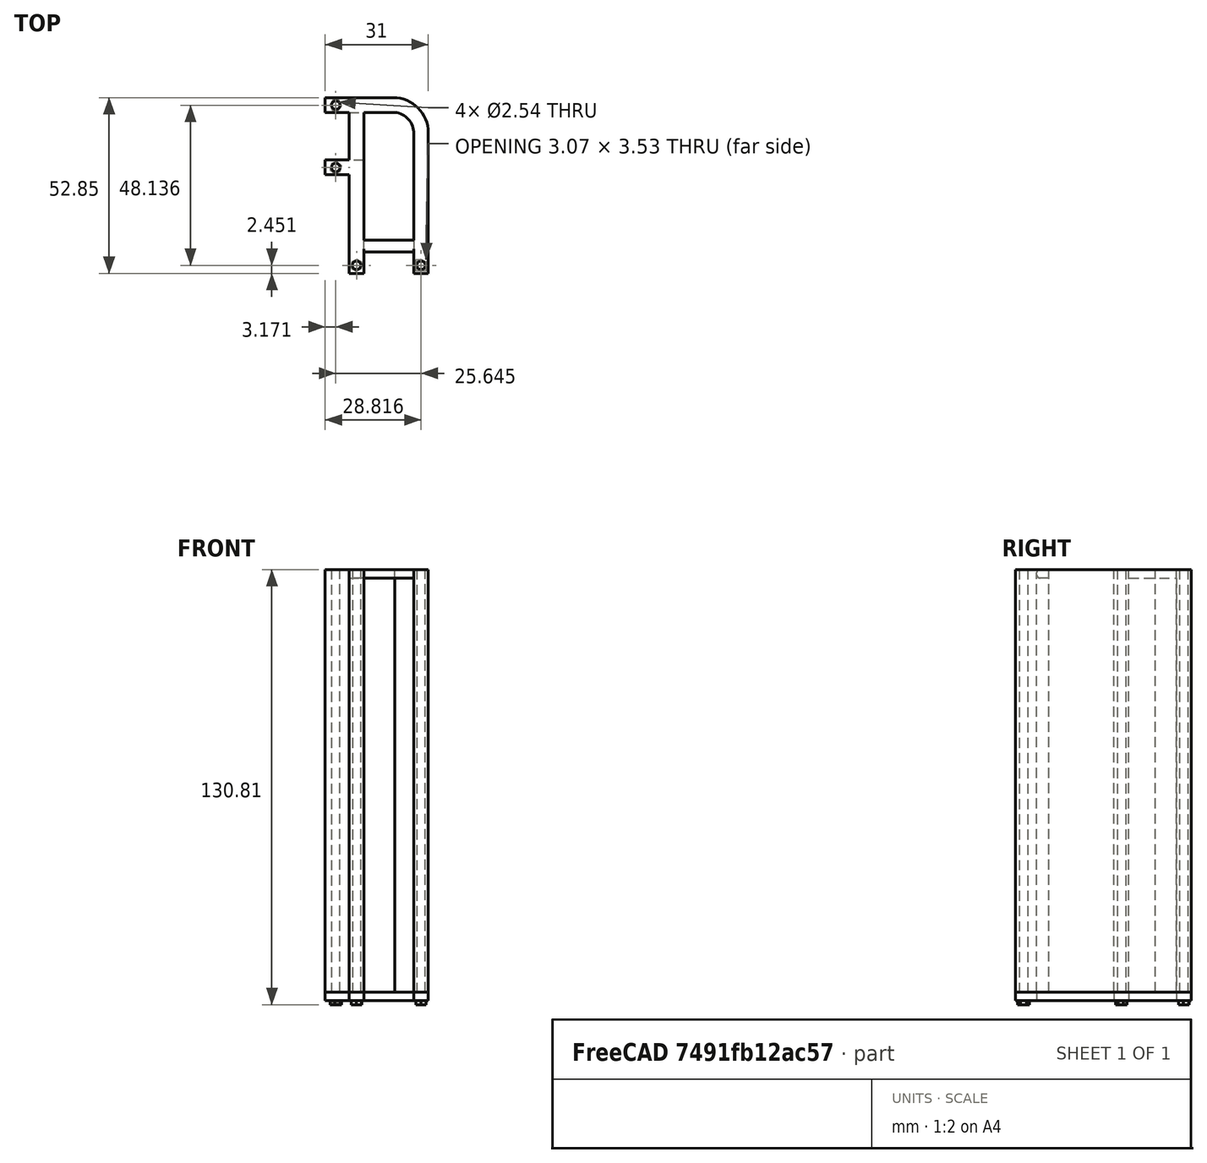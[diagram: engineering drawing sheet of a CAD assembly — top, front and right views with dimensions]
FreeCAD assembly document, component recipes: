
FREECAD ASSEMBLY — COMPONENT RECIPES ("mrscoopy_test")

This assembly document has 2 components, labeled P0..P1 below (a component is one placed body or linked part). 2 of them carry a construction recipe — the FreeCAD feature program that regenerates the part from scratch, quoted from this document or its linked companion documents; the rest are supplied as boundary geometry only. No exploded tour is included for this assembly.
COMPONENT P0 — recipe-attached ("Body", modeled in this document).
Construction recipe (the document's own serialized feature program — sketch geometry with constraints, then the solid features built on it; lengths are millimeters unless a unit is written):

FEATURE [Sketcher::SketchObject] Sketch
  FullyConstrained = false
  MapMode = 5
  Support = -> [XY_Plane]
  sketch-geometry (26):
    g0: LineSegment StartX=0 StartY=26.6063 StartZ=0 EndX=-7.16788 EndY=26.6063 EndZ=0
    g1: LineSegment StartX=-7.16788 StartY=26.6063 StartZ=0 EndX=-7.16788 EndY=31.0413 EndZ=0
    g2: LineSegment StartX=-7.16788 StartY=31.0413 StartZ=0 EndX=13.2403 EndY=31.0413 EndZ=0
    g3: ArcOfCircle CenterX=13.2403 CenterY=20.4538 CenterZ=0 NormalX=0 NormalY=0 NormalZ=1 AngleXU=0 Radius=10.5875 StartAngle=2e-16 EndAngle=1.5708
    g4: LineSegment StartX=23.8278 StartY=20.4538 StartZ=0 EndX=23.8278 EndY=-21.8072 EndZ=0
    g5: LineSegment StartX=23.8278 StartY=-21.8072 StartZ=0 EndX=19.3928 EndY=-21.8072 EndZ=0
    g6: LineSegment StartX=19.3928 StartY=-21.8072 StartZ=0 EndX=19.3928 EndY=-15.4126 EndZ=0
    g7: LineSegment StartX=19.3928 StartY=-15.4126 StartZ=0 EndX=4.43503 EndY=-15.4126 EndZ=0
    g8: LineSegment StartX=4.43503 StartY=-15.4126 StartZ=0 EndX=4.43503 EndY=-21.78 EndZ=0
    g9: LineSegment StartX=4.43503 StartY=-21.78 StartZ=0 EndX=0 EndY=-21.78 EndZ=0
    g10: LineSegment StartX=0 StartY=26.6063 StartZ=0 EndX=0 EndY=12.274 EndZ=0
    g11: LineSegment StartX=0 StartY=12.274 StartZ=0 EndX=-7.16788 EndY=12.274 EndZ=0
    g12: LineSegment StartX=-7.16788 StartY=12.274 StartZ=0 EndX=-7.16788 EndY=7.839 EndZ=0
    g13: LineSegment StartX=-7.16788 StartY=7.839 StartZ=0 EndX=0 EndY=7.839 EndZ=0
    g14: LineSegment StartX=0 StartY=7.839 StartZ=0 EndX=0 EndY=-21.78 EndZ=0
    g15: LineSegment StartX=19.3928 StartY=20.1836 StartZ=0 EndX=19.3928 EndY=-11.8217 EndZ=0
    g16: LineSegment StartX=19.3928 StartY=-11.8217 StartZ=0 EndX=4.43503 EndY=-11.8217 EndZ=0
    g17: LineSegment StartX=4.43503 StartY=-11.8217 StartZ=0 EndX=4.43503 EndY=26.5927 EndZ=0
    g18: LineSegment StartX=4.43503 StartY=26.5927 StartZ=0 EndX=13.7304 EndY=26.5927 EndZ=0
    g19: ArcOfCircle CenterX=13.2403 CenterY=20.4538 CenterZ=0 NormalX=0 NormalY=0 NormalZ=1 AngleXU=0 Radius=6.15845 StartAngle=6.23931 EndAngle=7.77431
    g20: Circle CenterX=-3.99854 CenterY=28.777 CenterZ=0 NormalX=0 NormalY=0 NormalZ=1 AngleXU=0 Radius=1.27118
    g21: Circle CenterX=-3.99854 CenterY=10.0357 CenterZ=0 NormalX=0 NormalY=0 NormalZ=1 AngleXU=0 Radius=1.27118
    g22: Circle CenterX=2.26851 CenterY=-19.3586 CenterZ=0 NormalX=0 NormalY=0 NormalZ=1 AngleXU=0 Radius=1.27118
    g23: Circle CenterX=21.6462 CenterY=-19.3586 CenterZ=0 NormalX=0 NormalY=0 NormalZ=1 AngleXU=0 Radius=1.27118
    g24: LineSegment StartX=2.26851 StartY=-19.3586 StartZ=0 EndX=21.6462 EndY=-19.3586 EndZ=0
    g25: LineSegment StartX=-3.99854 StartY=10.0357 StartZ=0 EndX=-3.99854 EndY=28.777 EndZ=0
  constraints (55):
    c: PointOnObject(g0,g-2)
    c: Horizontal(g0)
    c: Coincident(g0,g1)
    c: Vertical(g1)
    c: Coincident(g1,g2)
    c: Horizontal(g2)
    c: Coincident(g3,g2)
    c: Tangent(g3,g4) = 1.5708
    c: Coincident(g4,g5)
    c: Horizontal(g5)
    c: Coincident(g5,g6)
    c: Vertical(g6)
    c: Coincident(g6,g7)
    c: Horizontal(g7)
    c: Coincident(g7,g8)
    c: Vertical(g8)
    c: Coincident(g8,g9)
    c: PointOnObject(g9,g-2)
    c: Horizontal(g9)
    c: Vertical(g4)
    c: Equal(g5,g9)
    c: Equal(g1,g5)
    c: Tangent(g3,g2)
    c: Coincident(g0,g10)
    c: PointOnObject(g10,g-2)
    c: Coincident(g10,g11)
    c: Horizontal(g11)
    c: Coincident(g11,g12)
    c: Vertical(g12)
    c: Coincident(g12,g13)
    c: PointOnObject(g13,g-2)
    c: Horizontal(g13)
    c: Coincident(g14,g9)
    c: Coincident(g15,g16)
    c: Horizontal(g16)
    c: Coincident(g16,g17)
    c: Coincident(g18,g17)
    c: Horizontal(g18)
    c: Coincident(g19,g3)
    c: Coincident(g19,g18)
    c: Coincident(g19,g15)
    c: Tangent(g17,g8)
    c: Tangent(g15,g6)
    c: Equal(g0,g11)
    c: Equal(g12,g1)
    c: Equal(g20,g21)
    c: Equal(g20,g22)
    c: Equal(g20,g23)
    c: Coincident(g24,g22)
    c: Coincident(g24,g23)
    c: Horizontal(g24)
    c: Coincident(g25,g21)
    c: Coincident(g25,g20)
    c: Vertical(g25)
    c: Coincident(g14,g13)
FEATURE [PartDesign::Pad] Pad
  Direction = (0,0,1)
  Length = 127
  Length2 = 10
  Profile = -> Sketch
  ReferenceAxis = -> Sketch [N_Axis]
  Type = 0
FEATURE [Sketcher::SketchObject] Sketch001
  FullyConstrained = false
  MapMode = 5
  Support = -> [XY_Plane]
  sketch-geometry (8):
    g0: LineSegment StartX=0 StartY=26.6033 StartZ=0 EndX=4.4361 EndY=26.6033 EndZ=0
    g1: LineSegment StartX=4.4361 StartY=26.6033 StartZ=0 EndX=4.4361 EndY=12.2559 EndZ=0
    g2: LineSegment StartX=4.4361 StartY=12.2559 StartZ=0 EndX=0 EndY=12.2559 EndZ=0
    g3: LineSegment StartX=0 StartY=12.2559 StartZ=0 EndX=0 EndY=26.6033 EndZ=0
    g4: LineSegment StartX=4.4361 StartY=-11.8217 StartZ=0 EndX=19.3928 EndY=-11.8217 EndZ=0
    g5: LineSegment StartX=19.3928 StartY=-11.8217 StartZ=0 EndX=19.3928 EndY=-15.4126 EndZ=0
    g6: LineSegment StartX=19.3928 StartY=-15.4126 StartZ=0 EndX=4.4361 EndY=-15.4126 EndZ=0
    g7: LineSegment StartX=4.4361 StartY=-15.4126 StartZ=0 EndX=4.4361 EndY=-11.8217 EndZ=0
  constraints (17):
    c: PointOnObject(g0,g-2)
    c: Coincident(g0,g1)
    c: Coincident(g1,g2)
    c: Coincident(g2,g3)
    c: Coincident(g3,g0)
    c: Horizontal(g0)
    c: Horizontal(g2)
    c: Vertical(g1)
    c: Vertical(g3)
    c: Coincident(g4,g5)
    c: Coincident(g5,g6)
    c: Coincident(g6,g7)
    c: Coincident(g7,g4)
    c: Horizontal(g4)
    c: Horizontal(g6)
    c: Vertical(g5)
    c: Vertical(g7)
FEATURE [PartDesign::Pocket] Pocket
  BaseFeature = -> Pad
  Direction = (0,0,-1)
  Length = 124.46
  Length2 = 5
  Profile = -> Sketch001
  ReferenceAxis = -> Sketch001 [N_Axis]
  Reversed = true
  Type = 0
FEATURE [PartDesign::CoordinateSystem] Local_CS
  AttacherType = Attacher::AttachEngine3D
  MapMode = 5
  Support = -> [XY_Plane]
FEATURE [PartDesign::Fillet] Fillet
  Base = -> Pocket [Edge72,Edge31]
  BaseFeature = -> Pocket
  Radius = 0.9906
  SupportTransform = false
  UseAllEdges = false
FEATURE [PartDesign::Body] Body
  Group = -> [Sketch,Pad,Sketch001,Pocket,Local_CS,Fillet]
  Origin = -> Origin
  Tip = -> Fillet
COMPONENT P1 — recipe-attached ("Body004", modeled in this document).
Construction recipe (the document's own serialized feature program — sketch geometry with constraints, then the solid features built on it; lengths are millimeters unless a unit is written):

FEATURE [Sketcher::SketchObject] Sketch003
  FullyConstrained = false
  MapMode = 5
  Support = -> [XY_Plane002]
  sketch-geometry (21):
    g0: LineSegment StartX=0 StartY=26.6063 StartZ=0 EndX=-7.16788 EndY=26.6063 EndZ=0
    g1: LineSegment StartX=-7.16788 StartY=26.6063 StartZ=0 EndX=-7.16788 EndY=31.0413 EndZ=0
    g2: LineSegment StartX=-7.16788 StartY=31.0413 StartZ=0 EndX=13.2403 EndY=31.0413 EndZ=0
    g3: ArcOfCircle CenterX=13.2403 CenterY=20.4538 CenterZ=0 NormalX=0 NormalY=0 NormalZ=1 AngleXU=0 Radius=10.5875 StartAngle=2e-16 EndAngle=1.5708
    g4: LineSegment StartX=23.8278 StartY=20.4538 StartZ=0 EndX=23.8278 EndY=-21.8072 EndZ=0
    g5: LineSegment StartX=23.8278 StartY=-21.8072 StartZ=0 EndX=19.3928 EndY=-21.8072 EndZ=0
    g6: LineSegment StartX=19.3928 StartY=-21.8072 StartZ=0 EndX=19.3928 EndY=-15.4126 EndZ=0
    g7: LineSegment StartX=19.3928 StartY=-15.4126 StartZ=0 EndX=4.43503 EndY=-15.4126 EndZ=0
    g8: LineSegment StartX=4.43503 StartY=-15.4126 StartZ=0 EndX=4.43503 EndY=-21.78 EndZ=0
    g9: LineSegment StartX=4.43503 StartY=-21.78 StartZ=0 EndX=0 EndY=-21.78 EndZ=0
    g10: LineSegment StartX=0 StartY=26.6063 StartZ=0 EndX=0 EndY=12.274 EndZ=0
    g11: LineSegment StartX=0 StartY=12.274 StartZ=0 EndX=-7.16788 EndY=12.274 EndZ=0
    g12: LineSegment StartX=-7.16788 StartY=12.274 StartZ=0 EndX=-7.16788 EndY=7.839 EndZ=0
    g13: LineSegment StartX=-7.16788 StartY=7.839 StartZ=0 EndX=0 EndY=7.839 EndZ=0
    g14: LineSegment StartX=0 StartY=7.839 StartZ=0 EndX=0 EndY=-21.78 EndZ=0
    g15: Circle CenterX=-3.99854 CenterY=28.777 CenterZ=0 NormalX=0 NormalY=0 NormalZ=1 AngleXU=0 Radius=1.27118
    g16: Circle CenterX=-3.99854 CenterY=10.0357 CenterZ=0 NormalX=0 NormalY=0 NormalZ=1 AngleXU=0 Radius=1.27118
    g17: Circle CenterX=2.26851 CenterY=-19.3586 CenterZ=0 NormalX=0 NormalY=0 NormalZ=1 AngleXU=0 Radius=1.27118
    g18: Circle CenterX=21.6462 CenterY=-19.3586 CenterZ=0 NormalX=0 NormalY=0 NormalZ=1 AngleXU=0 Radius=1.27118
    g19: LineSegment StartX=2.26851 StartY=-19.3586 StartZ=0 EndX=21.6462 EndY=-19.3586 EndZ=0
    g20: LineSegment StartX=-3.99854 StartY=10.0357 StartZ=0 EndX=-3.99854 EndY=28.777 EndZ=0
  constraints (45):
    c: PointOnObject(g0,g-2)
    c: Horizontal(g0)
    c: Coincident(g0,g1)
    c: Vertical(g1)
    c: Coincident(g1,g2)
    c: Horizontal(g2)
    c: Coincident(g3,g2)
    c: Tangent(g3,g4) = 1.5708
    c: Coincident(g4,g5)
    c: Horizontal(g5)
    c: Coincident(g5,g6)
    c: Vertical(g6)
    c: Coincident(g6,g7)
    c: Horizontal(g7)
    c: Coincident(g7,g8)
    c: Vertical(g8)
    c: Coincident(g8,g9)
    c: PointOnObject(g9,g-2)
    c: Horizontal(g9)
    c: Vertical(g4)
    c: Equal(g5,g9)
    c: Equal(g1,g5)
    c: Tangent(g3,g2)
    c: Coincident(g0,g10)
    c: PointOnObject(g10,g-2)
    c: Coincident(g10,g11)
    c: Horizontal(g11)
    c: Coincident(g11,g12)
    c: Vertical(g12)
    c: Coincident(g12,g13)
    c: PointOnObject(g13,g-2)
    c: Horizontal(g13)
    c: Coincident(g14,g9)
    c: Equal(g0,g11)
    c: Equal(g12,g1)
    c: Equal(g15,g16)
    c: Equal(g15,g17)
    c: Equal(g15,g18)
    c: Coincident(g19,g17)
    c: Coincident(g19,g18)
    c: Horizontal(g19)
    c: Coincident(g20,g16)
    c: Coincident(g20,g15)
    c: Vertical(g20)
    c: Coincident(g14,g13)
FEATURE [PartDesign::Pad] Pad001
  Direction = (0,0,1)
  Length = 2.54
  Length2 = 10
  Profile = -> Sketch003
  ReferenceAxis = -> Sketch003 [N_Axis]
  Reversed = true
  Type = 0
FEATURE [Sketcher::SketchObject] Sketch004
  FullyConstrained = false
  MapMode = 5
  Support = -> [XY_Plane002]
  sketch-geometry (32):
    g0: Circle CenterX=-3.99854 CenterY=28.777 CenterZ=0 NormalX=0 NormalY=0 NormalZ=1 AngleXU=0 Radius=1.27118
    g1: Circle CenterX=-3.99854 CenterY=10.0357 CenterZ=0 NormalX=0 NormalY=0 NormalZ=1 AngleXU=0 Radius=1.27118
    g2: Circle CenterX=2.26851 CenterY=-19.3586 CenterZ=0 NormalX=0 NormalY=0 NormalZ=1 AngleXU=0 Radius=1.27118
    g3: Circle CenterX=21.6462 CenterY=-19.3586 CenterZ=0 NormalX=0 NormalY=0 NormalZ=1 AngleXU=0 Radius=1.27118
    g4: LineSegment StartX=-2.99658 StartY=30.2291 StartZ=0 EndX=-4.75513 EndY=30.3708 EndZ=0
    g5: LineSegment StartX=-4.75513 StartY=30.3708 StartZ=0 EndX=-5.75709 EndY=28.9187 EndZ=0
    g6: LineSegment StartX=-5.75709 StartY=28.9187 StartZ=0 EndX=-5.0005 EndY=27.3249 EndZ=0
    g7: LineSegment StartX=-5.0005 StartY=27.3249 StartZ=0 EndX=-3.24195 EndY=27.1832 EndZ=0
    g8: LineSegment StartX=-3.24195 StartY=27.1832 StartZ=0 EndX=-2.23999 EndY=28.6353 EndZ=0
    g9: LineSegment StartX=-2.23999 StartY=28.6353 StartZ=0 EndX=-2.99658 EndY=30.2291 EndZ=0
    g10: Circle CenterX=-3.99854 CenterY=28.777 CenterZ=0 NormalX=0 NormalY=0 NormalZ=1 AngleXU=0 Radius=1.76425
    g11: LineSegment StartX=-4.33287 StartY=8.3034 StartZ=0 EndX=-2.6655 EndY=8.88 EndZ=0
    g12: LineSegment StartX=-2.6655 StartY=8.88 StartZ=0 EndX=-2.33117 EndY=10.6123 EndZ=0
    g13: LineSegment StartX=-2.33117 StartY=10.6123 StartZ=0 EndX=-3.66421 EndY=11.768 EndZ=0
    g14: LineSegment StartX=-3.66421 StartY=11.768 StartZ=0 EndX=-5.33157 EndY=11.1914 EndZ=0
    g15: LineSegment StartX=-5.33157 StartY=11.1914 StartZ=0 EndX=-5.6659 EndY=9.45907 EndZ=0
    g16: LineSegment StartX=-5.6659 StartY=9.45907 StartZ=0 EndX=-4.33287 EndY=8.3034 EndZ=0
    g17: Circle CenterX=-3.99854 CenterY=10.0357 CenterZ=0 NormalX=0 NormalY=0 NormalZ=1 AngleXU=0 Radius=1.76425
    g18: LineSegment StartX=2.33191 StartY=-17.5955 StartZ=0 EndX=0.773315 EndY=-18.4221 EndZ=0
    g19: LineSegment StartX=0.773315 StartY=-18.4221 StartZ=0 EndX=0.709916 EndY=-20.1852 EndZ=0
    g20: LineSegment StartX=0.709916 StartY=-20.1852 StartZ=0 EndX=2.20511 EndY=-21.1217 EndZ=0
    g21: LineSegment StartX=2.20511 StartY=-21.1217 StartZ=0 EndX=3.76371 EndY=-20.2951 EndZ=0
    g22: LineSegment StartX=3.76371 StartY=-20.2951 StartZ=0 EndX=3.82711 EndY=-18.5319 EndZ=0
    g23: LineSegment StartX=3.82711 StartY=-18.5319 StartZ=0 EndX=2.33191 EndY=-17.5955 EndZ=0
    g24: Circle CenterX=2.26851 CenterY=-19.3586 CenterZ=0 NormalX=0 NormalY=0 NormalZ=1 AngleXU=0 Radius=1.76425
    g25: LineSegment StartX=23.1676 StartY=-18.4653 StartZ=0 EndX=21.6333 EndY=-17.5944 EndZ=0
    g26: LineSegment StartX=21.6333 StartY=-17.5944 StartZ=0 EndX=20.1119 EndY=-18.4877 EndZ=0
    g27: LineSegment StartX=20.1119 StartY=-18.4877 StartZ=0 EndX=20.1249 EndY=-20.2519 EndZ=0
    g28: LineSegment StartX=20.1249 StartY=-20.2519 StartZ=0 EndX=21.6592 EndY=-21.1228 EndZ=0
    g29: LineSegment StartX=21.6592 StartY=-21.1228 StartZ=0 EndX=23.1806 EndY=-20.2295 EndZ=0
    g30: LineSegment StartX=23.1806 StartY=-20.2295 StartZ=0 EndX=23.1676 EndY=-18.4653 EndZ=0
    g31: Circle CenterX=21.6462 CenterY=-19.3586 CenterZ=0 NormalX=0 NormalY=0 NormalZ=1 AngleXU=0 Radius=1.76425
  constraints (66):
    c: Equal(g0,g1)
    c: Equal(g0,g2)
    c: Equal(g0,g3)
    c: Block(g0)
    c: Block(g1)
    c: Block(g3)
    c: Block(g2)
    c: Coincident(g4,g5)
    c: Coincident(g5,g6)
    c: Coincident(g6,g7)
    c: Coincident(g7,g8)
    c: Coincident(g8,g9)
    c: Coincident(g9,g4)
    c: Equal(g4, g5-g9) x5
    c: PointOnObject(g4,g10)
    c: PointOnObject(g5,g10)
    c: PointOnObject(g6,g10)
    c: PointOnObject(g7,g10)
    c: PointOnObject(g8,g10)
    c: PointOnObject(g9,g10)
    c: Coincident(g10,g0)
    c: Coincident(g11,g12)
    c: Coincident(g12,g13)
    c: Coincident(g13,g14)
    c: Coincident(g14,g15)
    c: Coincident(g15,g16)
    c: Coincident(g16,g11)
    c: Equal(g11, g12-g16) x5
    c: PointOnObject(g11,g17)
    c: PointOnObject(g12,g17)
    c: PointOnObject(g13,g17)
    c: PointOnObject(g14,g17)
    c: PointOnObject(g15,g17)
    c: PointOnObject(g16,g17)
    c: Coincident(g17,g1)
    c: Coincident(g18,g19)
    c: Coincident(g19,g20)
    c: Coincident(g20,g21)
    c: Coincident(g21,g22)
    c: Coincident(g22,g23)
    c: Coincident(g23,g18)
    c: Equal(g18, g19-g23) x5
    c: PointOnObject(g18,g24)
    c: PointOnObject(g19,g24)
    c: PointOnObject(g20,g24)
    c: PointOnObject(g21,g24)
    c: PointOnObject(g22,g24)
    c: PointOnObject(g23,g24)
    c: Coincident(g24,g2)
    c: Coincident(g25,g26)
    c: Coincident(g26,g27)
    c: Coincident(g27,g28)
    c: Coincident(g28,g29)
    c: Coincident(g29,g30)
    c: Coincident(g30,g25)
    c: Equal(g25, g26-g30) x5
    c: PointOnObject(g25,g31)
    c: PointOnObject(g26,g31)
    c: PointOnObject(g27,g31)
    c: PointOnObject(g28,g31)
    c: PointOnObject(g29,g31)
    c: PointOnObject(g30,g31)
    c: Coincident(g31,g3)
    c: Equal(g10,g17)
    c: Equal(g17,g24)
    c: Equal(g24,g31)
FEATURE [PartDesign::Pad] Pad002
  BaseFeature = -> Pad001
  Direction = (0,0,1)
  Length = 3.81
  Length2 = 10
  Profile = -> Sketch004
  ReferenceAxis = -> Sketch004 [N_Axis]
  Reversed = true
  Type = 0
FEATURE [PartDesign::CoordinateSystem] Local_CS001
  AttacherType = Attacher::AttachEngine3D
  MapMode = 2
FEATURE [PartDesign::Body] Body004
  Group = -> [Sketch003,Pad001,Sketch004,Pad002,Local_CS001]
  Origin = -> Origin002
  Tip = -> Pad002
PROVENANCE & LICENSES
A FreeCAD (.FCStd) document from a public repository crawl; recipes are the document's own serialized feature recipes (and, for linked parts, companion documents' recipes).
License: as declared in the source repository (recorded in the dataset sidecar).
